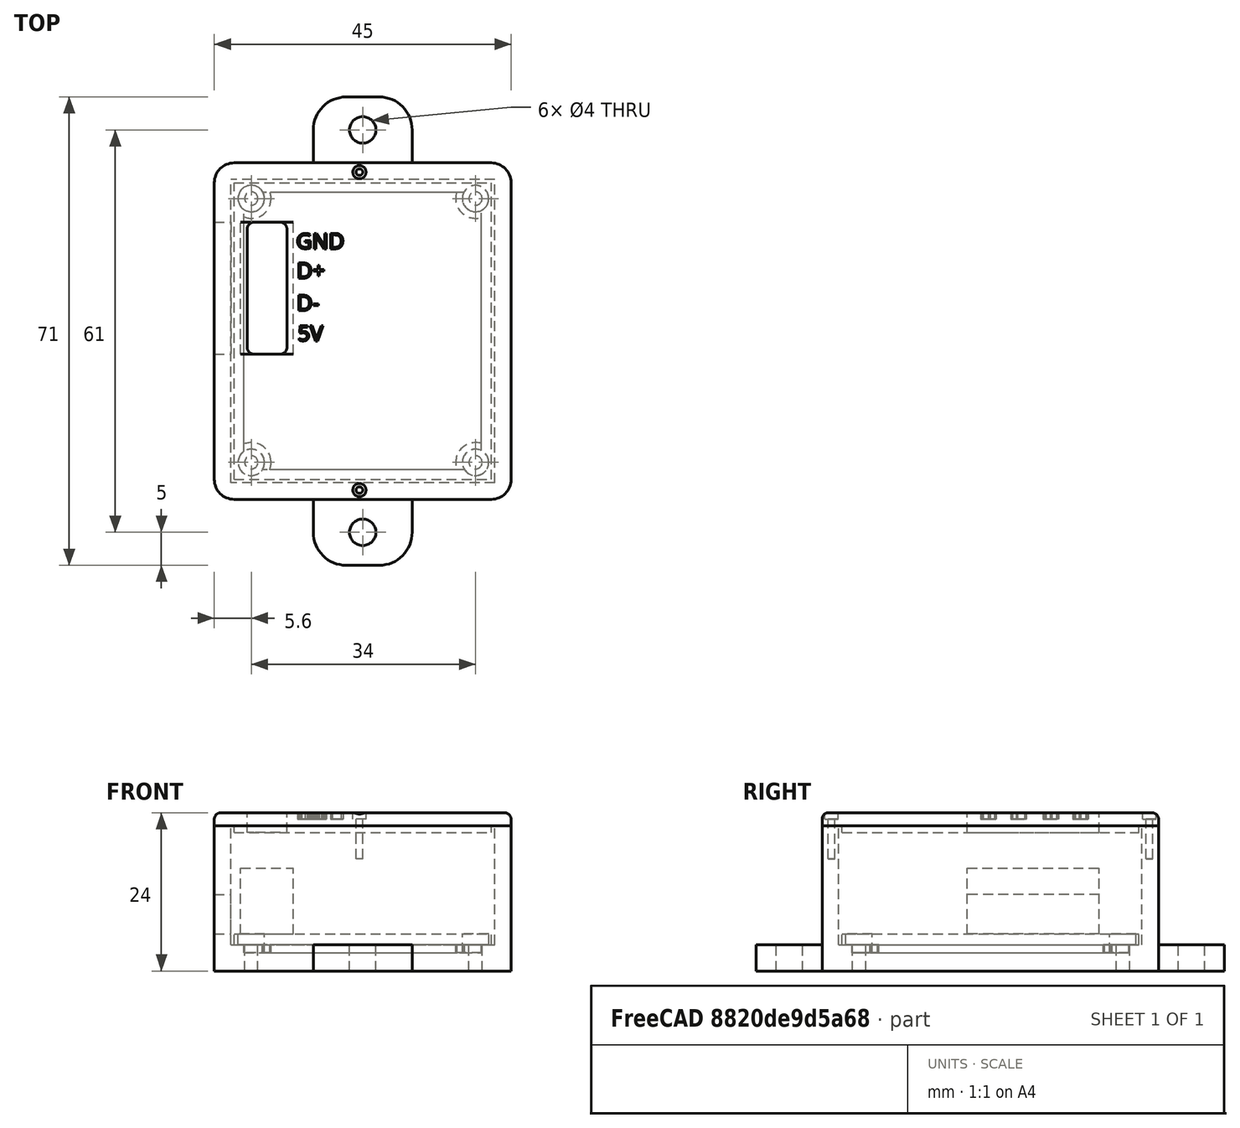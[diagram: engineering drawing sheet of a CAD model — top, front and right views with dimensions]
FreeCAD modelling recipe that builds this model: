
FCSTD DOCUMENT  (FreeCAD 0.17R13522 (Git))
Label: Caja Bridge TCP-RTU V1
License: All rights reserved
LicenseURL: http://en.wikipedia.org/wiki/All_rights_reserved
objects: Part::Cylinder×20, Part::Box×12, Part::MultiFuse×12, Part::Cut×11, Part::Fillet×5, Part::Part2DObjectPython×4, Part::Extrusion×4
note: 68 computed .brp shape members not serialized (recipe doc carries the construction recipe); baked Part::Feature solids carry a one-line shape summary decoded from their .brp

FEATURE [Part::Box] Box  label="Cubo"
  AttacherType = Attacher::AttachEngine3D
  Height = 1.6
  Length = 39
  Width = 45
FEATURE [Part::Cylinder] Cylinder  label="Cilindro"
  Angle = 360
  AttacherType = Attacher::AttachEngine3D
  Height = 10
  Placement = pos=(2.6,2.6,-5) rot=(0,0,1;0rad)
  Radius = 2
FEATURE [Part::Cylinder] Cylinder001  label="Cilindro001"
  Angle = 360
  AttacherType = Attacher::AttachEngine3D
  Height = 10
  Placement = pos=(36.6,2.6,-5) rot=(0,0,1;0rad)
  Radius = 2
FEATURE [Part::Cylinder] Cylinder002  label="Cilindro002"
  Angle = 360
  AttacherType = Attacher::AttachEngine3D
  Height = 10
  Placement = pos=(36.6,42.6,-5) rot=(0,0,1;0rad)
  Radius = 2
FEATURE [Part::Cylinder] Cylinder003  label="Cilindro003"
  Angle = 360
  AttacherType = Attacher::AttachEngine3D
  Height = 10
  Placement = pos=(2.6,42.6,-5) rot=(0,0,1;0rad)
  Radius = 2
FEATURE [Part::Box] Box001  label="Cubo001"
  AttacherType = Attacher::AttachEngine3D
  Height = 10
  Length = 8
  Placement = pos=(1,19,1.6) rot=(0,0,1;0rad)
  Width = 20
FEATURE [Part::Box] Box002  label="Cubo002"
  AttacherType = Attacher::AttachEngine3D
  Height = 20
  Length = 40
  Placement = pos=(-0.5,-0.5,0) rot=(0,0,1;0rad)
  Width = 46
FEATURE [Part::Box] Box003  label="Cubo003"
  AttacherType = Attacher::AttachEngine3D
  Height = 22
  Length = 45
  Placement = pos=(-3,-3,-4) rot=(0,0,1;0rad)
  Width = 51
FEATURE [Part::Box] Box004  label="Cubo004"
  AttacherType = Attacher::AttachEngine3D
  Height = 1.5
  Length = 36
  Placement = pos=(1.5,1.5,-1.2) rot=(0,0,1;0rad)
  Width = 42
FEATURE [Part::MultiFuse] Fusion
  Refine = true
  Shapes = -> [Box,Box004]
FEATURE [Part::MultiFuse] Fusion001
  Refine = true
  Shapes = -> [Fusion,Box001]
FEATURE [Part::MultiFuse] Fusion002
  Refine = true
  Shapes = -> [Cylinder,Cylinder003,Cylinder002,Cylinder001]
FEATURE [Part::Cut] Cut  label="Electronica"
  Base = -> Fusion001
  Refine = true
  Tool = -> Fusion002
FEATURE [Part::Box] Box005  label="Cubo005"
  AttacherType = Attacher::AttachEngine3D
  Height = 1.5
  Length = 36
  Placement = pos=(1.5,1.5,-1.2) rot=(0,0,1;0rad)
  Width = 42
FEATURE [Part::MultiFuse] Fusion003
  Refine = true
  Shapes = -> [Box002,Box005]
FEATURE [Part::Box] Box006  label="Cubo006"
  AttacherType = Attacher::AttachEngine3D
  Height = 6
  Length = 22
  Placement = pos=(-10,19,1.6) rot=(0,0,1;0rad)
  Width = 20
FEATURE [Part::Box] Box007  label="Cubo007"
  AttacherType = Attacher::AttachEngine3D
  Height = 2
  Length = 45
  Placement = pos=(-3,-3,18) rot=(0,0,1;0rad)
  Width = 51
FEATURE [Part::Box] Box008  label="Cubo008"
  AttacherType = Attacher::AttachEngine3D
  Height = 3
  Length = 39
  Placement = pos=(0,0,17) rot=(0,0,1;0rad)
  Width = 45
FEATURE [Part::Cylinder] Cylinder004  label="Cilindro004"
  Angle = 360
  AttacherType = Attacher::AttachEngine3D
  Height = 10
  Placement = pos=(2.6,2.6,-5) rot=(0,0,1;0rad)
  Radius = 1
FEATURE [Part::Cylinder] Cylinder005  label="Cilindro005"
  Angle = 360
  AttacherType = Attacher::AttachEngine3D
  Height = 10
  Placement = pos=(36.6,2.6,-5) rot=(0,0,1;0rad)
  Radius = 1
FEATURE [Part::Cylinder] Cylinder006  label="Cilindro006"
  Angle = 360
  AttacherType = Attacher::AttachEngine3D
  Height = 10
  Placement = pos=(36.6,42.6,-5) rot=(0,0,1;0rad)
  Radius = 1
FEATURE [Part::Cylinder] Cylinder007  label="Cilindro007"
  Angle = 360
  AttacherType = Attacher::AttachEngine3D
  Height = 10
  Placement = pos=(2.6,42.6,-5) rot=(0,0,1;0rad)
  Radius = 1
FEATURE [Part::Cylinder] Cylinder008  label="Cilindro008"
  Angle = 360
  AttacherType = Attacher::AttachEngine3D
  Height = 3
  Placement = pos=(2.6,42.6,-3) rot=(0,0,1;0rad)
  Radius = 3
FEATURE [Part::Cylinder] Cylinder009  label="Cilindro009"
  Angle = 360
  AttacherType = Attacher::AttachEngine3D
  Height = 3
  Placement = pos=(36.6,2.6,-3) rot=(0,0,1;0rad)
  Radius = 3
FEATURE [Part::Cylinder] Cylinder010  label="Cilindro010"
  Angle = 360
  AttacherType = Attacher::AttachEngine3D
  Height = 3
  Placement = pos=(2.6,2.6,-3) rot=(0,0,1;0rad)
  Radius = 3
FEATURE [Part::Cylinder] Cylinder011  label="Cilindro011"
  Angle = 360
  AttacherType = Attacher::AttachEngine3D
  Height = 3
  Placement = pos=(36.6,42.6,-3) rot=(0,0,1;0rad)
  Radius = 3
FEATURE [Part::Cut] Cut001
  Base = -> Box003
  Refine = true
  Tool = -> Fusion003
FEATURE [Part::Cut] Cut002
  Base = -> Cut001
  Refine = true
  Tool = -> Box006
FEATURE [Part::MultiFuse] Fusion005
  Refine = true
  Shapes = -> [Cylinder008,Cut002,Cylinder011,Cylinder010,Cylinder009]
FEATURE [Part::MultiFuse] Fusion006
  Refine = true
  Shapes = -> [Cylinder007,Cylinder005,Cylinder004,Cylinder006]
FEATURE [Part::Cut] Cut003  label="Caja"
  Base = -> Fusion005
  Refine = true
  Tool = -> Fusion006
FEATURE [Part::MultiFuse] Fusion007
  Refine = true
  Shapes = -> [Box007,Box008]
FEATURE [Part::Cylinder] Cylinder012  label="Cilindro012"
  Angle = 360
  AttacherType = Attacher::AttachEngine3D
  Height = 10
  Placement = pos=(19,-1.6,13) rot=(0,0,1;0rad)
  Radius = 0.5
FEATURE [Part::Cylinder] Cylinder013  label="Cilindro013"
  Angle = 360
  AttacherType = Attacher::AttachEngine3D
  Height = 10
  Placement = pos=(19,46.6,13) rot=(0,0,1;0rad)
  Radius = 0.5
FEATURE [Part::MultiFuse] Fusion008
  Refine = true
  Shapes = -> [Cylinder012,Cylinder013]
FEATURE [Part::Cylinder] Cylinder014  label="Cilindro014"
  Angle = 360
  AttacherType = Attacher::AttachEngine3D
  Height = 10
  Placement = pos=(19,46.6,13) rot=(0,0,1;0rad)
  Radius = 0.5
FEATURE [Part::Cylinder] Cylinder015  label="Cilindro015"
  Angle = 360
  AttacherType = Attacher::AttachEngine3D
  Height = 10
  Placement = pos=(19,-1.6,13) rot=(0,0,1;0rad)
  Radius = 0.5
FEATURE [Part::MultiFuse] Fusion009
  Refine = true
  Shapes = -> [Cylinder015,Cylinder014]
FEATURE [Part::Cylinder] Cylinder016  label="Cilindro016"
  Angle = 360
  AttacherType = Attacher::AttachEngine3D
  Height = 10
  Placement = pos=(19,-1.6,19) rot=(0,0,1;0rad)
  Radius = 1
FEATURE [Part::Cylinder] Cylinder017  label="Cilindro017"
  Angle = 360
  AttacherType = Attacher::AttachEngine3D
  Height = 10
  Placement = pos=(19,46.6,19) rot=(0,0,1;0rad)
  Radius = 1
FEATURE [Part::MultiFuse] Fusion010
  Refine = true
  Shapes = -> [Cylinder016,Cylinder017]
FEATURE [Part::Cut] Cut006
  Base = -> Cut003
  Refine = true
  Tool = -> Fusion008
FEATURE [Part::Box] Box009  label="Cubo009"
  AttacherType = Attacher::AttachEngine3D
  Height = 4
  Length = 15
  Placement = pos=(12,-13,-4) rot=(0,0,1;0rad)
  Width = 10
FEATURE [Part::Cylinder] Cylinder018  label="Cilindro018"
  Angle = 360
  AttacherType = Attacher::AttachEngine3D
  Height = 10
  Placement = pos=(19.5,-8,-7) rot=(0,0,1;0rad)
  Radius = 2
FEATURE [Part::Cut] Cut007
  Base = -> Box009
  Refine = true
  Tool = -> Cylinder018
FEATURE [Part::Cylinder] Cylinder019  label="Cilindro019"
  Angle = 360
  AttacherType = Attacher::AttachEngine3D
  Height = 10
  Placement = pos=(19.5,-8,-7) rot=(0,0,1;0rad)
  Radius = 2
FEATURE [Part::Box] Box010  label="Cubo010"
  AttacherType = Attacher::AttachEngine3D
  Height = 4
  Length = 15
  Placement = pos=(12,-13,-4) rot=(0,0,1;0rad)
  Width = 10
FEATURE [Part::Cut] Cut008
  Base = -> Box010
  Placement = pos=(0,61,0) rot=(0,0,1;0rad)
  Refine = true
  Tool = -> Cylinder019
FEATURE [Part::MultiFuse] Fusion011
  Refine = true
  Shapes = -> [Cut006,Cut008,Cut007]
FEATURE [Part::Fillet] Fillet001
  Base = -> Fusion011
  Edges = 4 edges r=5: [Edge38,Edge44,Edge61,Edge66]
FEATURE [Part::Fillet] Fillet002  label="Caja V1"
  Base = -> Fillet001
  Edges = 4 edges r=3: [Edge16,Edge18,Edge41,Edge50]
FEATURE [Part::Fillet] Fillet
  Base = -> Fusion007
  Edges = 4 edges r=3: [Edge1,Edge3,Edge6,Edge9]
FEATURE [Part::Fillet] Fillet003
  Base = -> Fillet
  Edges = 4 edges r=1: [Edge1,Edge7,Edge8,Edge11]
FEATURE [Part::Cut] Cut009
  Base = -> Fillet003
  Refine = true
  Tool = -> Fusion010
FEATURE [Part::Cut] Cut010  label="Tapa V2"
  Base = -> Cut009
  Refine = true
  Tool = -> Fusion009
FEATURE [Part::Box] Box011  label="Cubo011"
  AttacherType = Attacher::AttachEngine3D
  Height = 48
  Length = 6
  Placement = pos=(2,19,1.6) rot=(0,0,1;0rad)
  Width = 20
FEATURE [Part::Cut] Cut011
  Base = -> Cut010
  Refine = true
  Tool = -> Box011
FEATURE [Part::Fillet] Fillet004  label="tapa V1"
  Base = -> Cut011
  Edges = 4 edges r=1: [Edge75,Edge76,Edge78,Edge80]
FEATURE [Part::Part2DObjectPython] ShapeString  label="GND"  # Draft 2D object (typed FeaturePython)
  FontFile = <path>
  Placement = pos=(9.41125,34.9742,20) rot=(0,0,1;0rad)
  Size = 3
  String = GND
  Support = -> [Fillet004]
  Tracking = 0
FEATURE [Part::Part2DObjectPython] ShapeString001  # Draft 2D object (typed FeaturePython)
  FontFile = C:/Program Files/FreeCAD 0.17/OpenSans-Regular.ttf
  Placement = pos=(9.47171,30.4997,20) rot=(0,0,1;0rad)
  Size = 3
  String = D+
  Tracking = 0
FEATURE [Part::Part2DObjectPython] ShapeString002  # Draft 2D object (typed FeaturePython)
  FontFile = C:/Program Files/FreeCAD 0.17/OpenSans-Regular.ttf
  Placement = pos=(9.47171,25.6019,20) rot=(0,0,1;0rad)
  Size = 3
  String = D-
  Tracking = 0
FEATURE [Part::Part2DObjectPython] ShapeString003  # Draft 2D object (typed FeaturePython)
  FontFile = C:/Program Files/FreeCAD 0.17/OpenSans-Regular.ttf
  Placement = pos=(9.65311,21.0064,20) rot=(0,0,1;0rad)
  Size = 3
  String = 5V
  Support = -> [Fillet004]
  Tracking = 0
FEATURE [Part::Extrusion] Extrude
  Base = -> ShapeString
  Dir = (0,0,-1)
  DirMode = 0
  FaceMakerClass = Part::FaceMakerBullseye
  LengthFwd = 1
  LengthRev = 0
  Solid = true
  Symmetric = false
FEATURE [Part::Extrusion] Extrude001
  Base = -> ShapeString001
  Dir = (0,0,-1)
  DirMode = 0
  FaceMakerClass = Part::FaceMakerBullseye
  LengthFwd = 1
  LengthRev = 0
  Solid = true
  Symmetric = false
FEATURE [Part::Extrusion] Extrude002
  Base = -> ShapeString002
  Dir = (0,0,-1)
  DirMode = 0
  FaceMakerClass = Part::FaceMakerBullseye
  LengthFwd = 1
  LengthRev = 0
  Solid = true
  Symmetric = false
FEATURE [Part::Extrusion] Extrude003
  Base = -> ShapeString003
  Dir = (0,0,-1)
  DirMode = 0
  FaceMakerClass = Part::FaceMakerBullseye
  LengthFwd = 1
  LengthRev = 0
  Solid = true
  Symmetric = false
FEATURE [Part::MultiFuse] Fusion012
  Refine = true
  Shapes = -> [Extrude003,Extrude,Extrude001,Extrude002]
FEATURE [Part::Cut] Cut012  label="Tapa V1"
  Base = -> Fillet004
  Refine = true
  Tool = -> Fusion012
note: 1 file-system path scrubbed to <path> (originals preserved in the JSON sidecar)
